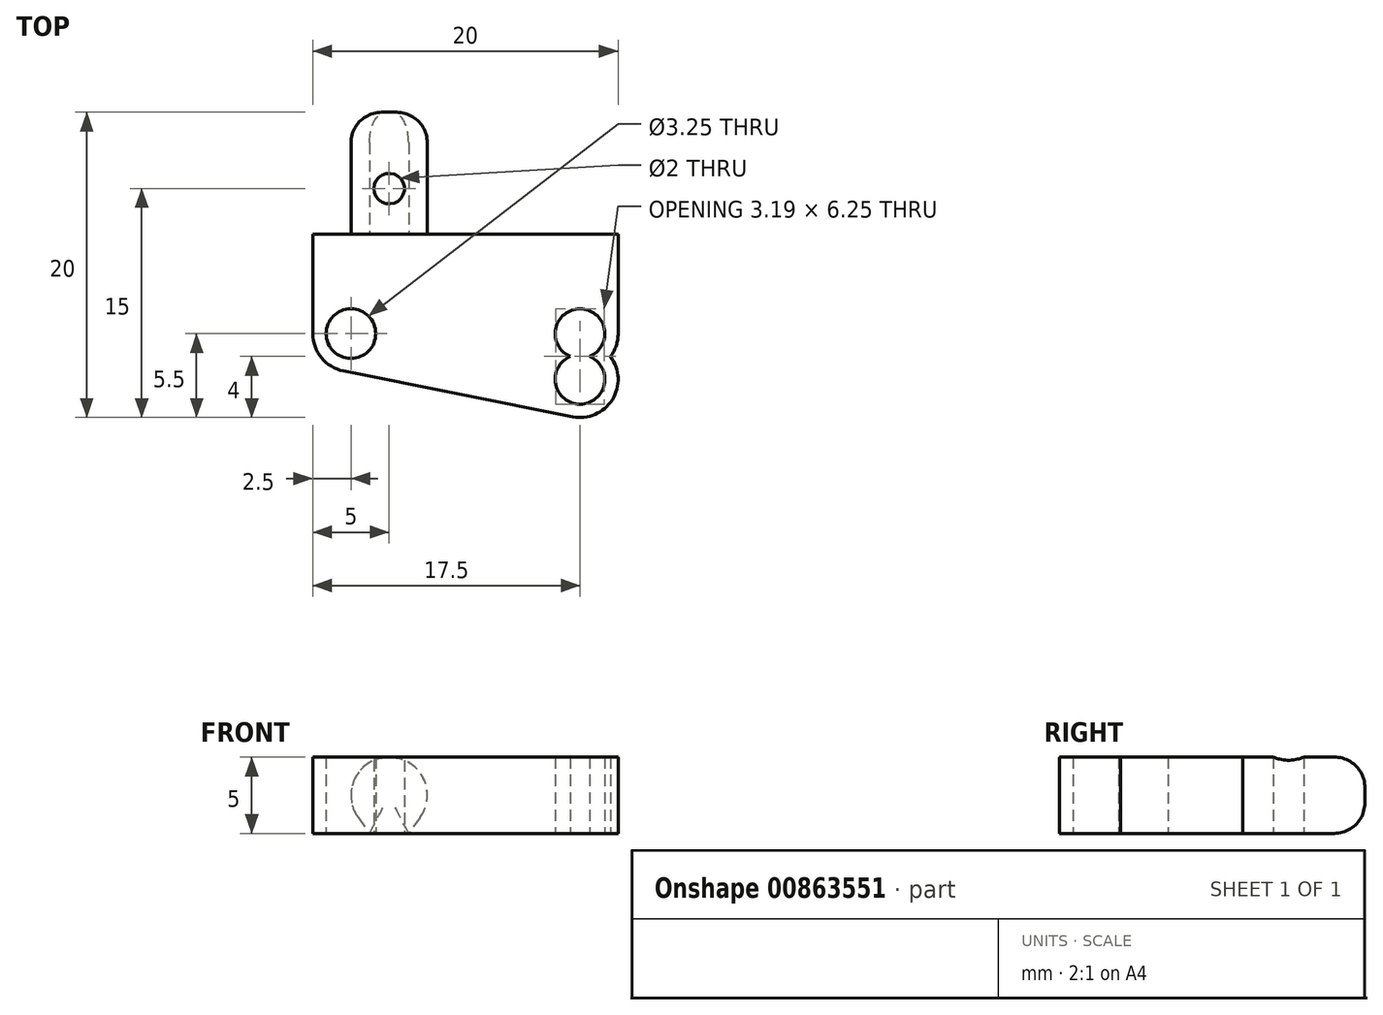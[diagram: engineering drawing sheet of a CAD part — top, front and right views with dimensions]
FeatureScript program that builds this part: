
annotation { "Feature Type Name" : "Feature", "Feature Type Description" : "" }
export const myFeature = defineFeature(function(context is Context, id is Id, definition is map)
    precondition{}
    {
        {
            var Q0;
            Q0=qCreatedBy(makeId("Top.planeOp"),FACE);
            var sketch = newSketch(context, id + "F0", { "sketchPlane" : qUnion([Q0])});
            skLineSegment(sketch, "E0", {"start": v(-7.5, 0) * mm, "end": v(7.5, 0) * mm, "construction": true});
            skCircle(sketch, "E1", {"center": v(-7.5, 0) * mm, "radius": 1.63 * mm});
            skArc(sketch, "E2", {"start": v(8.12, -1.5) * mm, "mid": v(7.5, 1.63) * mm, "end": v(6.87, -1.5) * mm});
            skArc(sketch, "E3", {"start": v(6.88, -1.5) * mm, "mid": v(7.5, -4.63) * mm, "end": v(8.12, -1.5) * mm});
            skLineSegment(sketch, "E4", {"start": v(7.5, -3) * mm, "end": v(7.5, 0) * mm, "construction": true});
            skArc(sketch, "E5", {"start": v(-10, 0) * mm, "mid": v(-9.43, -1.58) * mm, "end": v(-8, -2.45) * mm});
            skArc(sketch, "E6", {"start": v(9.5, -1.5) * mm, "mid": v(9.87, -0.8) * mm, "end": v(10, 0) * mm});
            skArc(sketch, "E7", {"start": v(7, -5.45) * mm, "mid": v(9.62, -4.33) * mm, "end": v(9.5, -1.5) * mm});
            skPoint(sketch, "E8", {"position": v(5.5, -1.5) * mm});
            skLineSegment(sketch, "E9", {"start": v(-8, -2.45) * mm, "end": v(7, -5.45) * mm});
            skLineSegment(sketch, "E10", {"start": v(-10, 6.5) * mm, "end": v(10, 6.5) * mm});
            skLineSegment(sketch, "E11", {"start": v(10, 6.5) * mm, "end": v(10, 0) * mm});
            skLineSegment(sketch, "E12", {"start": v(-10, 6.5) * mm, "end": v(-10, 0) * mm});
            skSolve(sketch);
        }
        {
            var Q0;
            Q0=makeQuery(id+"F0.imprint","IMPRINT",FACE,{"disambiguationData":[TD([[makeQuery(id+"F0.imprint","IMPRINT",EDGE,{"derivedFrom":sQuery(id+"F0.wireOp",EDGE,"E1")}),-1.0]])]});
            extrude(context, id + "F1", {"entities" : qUnion([Q0]), "depth" : 5 * mm, "offsetDistance" : 25 * mm});
        }
        {
            var Q0;
            Q0=makeQuery(id+"F1.opExtrude","SWEPT_FACE",FACE,{"disambiguationData":[OSD([sQuery(id+"F0.wireOp",EDGE,"E10")])]});
            var sketch = newSketch(context, id + "F2", { "sketchPlane" : qUnion([Q0])});
            skLineSegment(sketch, "E13", {"start": v(10, 2.5) * mm, "end": v(-10, 2.5) * mm, "construction": true});
            skArc(sketch, "E14", {"start": v(7.03, 1.03) * mm, "mid": v(5, 5) * mm, "end": v(2.97, 1.03) * mm});
            skLineSegment(sketch, "E15", {"start": v(2.97, 1.03) * mm, "end": v(3.72, 0) * mm});
            skLineSegment(sketch, "E16", {"start": v(7.03, 1.03) * mm, "end": v(6.28, 0) * mm});
            skLineSegment(sketch, "E17", {"start": v(5, 2.5) * mm, "end": v(5, 0) * mm, "construction": true});
            skLineSegment(sketch, "E18.0", {"start": v(10, 0) * mm, "end": v(6.28, 0) * mm});
            skLineSegment(sketch, "E19", {"start": v(6.28, 0) * mm, "end": v(3.72, 0) * mm});
            skLineSegment(sketch, "E20", {"start": v(3.72, 0) * mm, "end": v(-10, 0) * mm});
            skSolve(sketch);
        }
        {
            var Q0;
            Q0=makeQuery(id+"F2.imprint","IMPRINT",FACE,{"disambiguationData":[TD([[makeQuery(id+"F2.imprint","IMPRINT",EDGE,{"derivedFrom":sQuery(id+"F2.wireOp",EDGE,"E14")}),1.0]])]});
            extrude(context, id + "F3", {"entities" : qUnion([Q0]), "operationType" : NewBodyOperationType.ADD, "depth" : 8 * mm, "offsetDistance" : 25 * mm});
        }
        {
            var Q0;
            Q0=makeQuery(id+"F1.opExtrude","CAP_FACE",FACE,{"disambiguationData":[OSD([sQuery(id+"F0.wireOp",EDGE,"E1"),sQuery(id+"F0.wireOp",EDGE,"E2"),sQuery(id+"F0.wireOp",EDGE,"E3"),sQuery(id+"F0.wireOp",EDGE,"E5"),sQuery(id+"F0.wireOp",EDGE,"E6"),sQuery(id+"F0.wireOp",EDGE,"E7"),sQuery(id+"F0.wireOp",EDGE,"E9"),sQuery(id+"F0.wireOp",EDGE,"E10"),sQuery(id+"F0.wireOp",EDGE,"E11"),sQuery(id+"F0.wireOp",EDGE,"E12")])],"isStart":false});
            var sketch = newSketch(context, id + "F4", { "sketchPlane" : qUnion([Q0])});
            skLineSegment(sketch, "E21", {"start": v(-10, 5) * mm, "end": v(10, 5) * mm});
            skSolve(sketch);
        }
        {
            var Q0;
            Q0=makeQuery(id+"F3.opExtrude","CAP_FACE",FACE,{"disambiguationData":[OSD([sQuery(id+"F2.wireOp",EDGE,"E14"),sQuery(id+"F2.wireOp",EDGE,"E15"),sQuery(id+"F2.wireOp",EDGE,"E16"),sQuery(id+"F2.wireOp",EDGE,"E19")])],"isStart":false});
            fillet(context, id + "F5", {"entities" : qUnion([Q0]), "radius" : 2 * mm, "tangentPropagation" : true, "allowEdgeOverflow" : false});
        }
        {
            var Q0;
            Q0=makeQuery(id+"F3.boolean.opBoolean","MERGE",FACE,{"derivedFrom":[makeQuery(id+"F1.opExtrude","CAP_FACE",FACE,{"disambiguationData":[OSD([sQuery(id+"F0.wireOp",EDGE,"E1"),sQuery(id+"F0.wireOp",EDGE,"E2"),sQuery(id+"F0.wireOp",EDGE,"E3"),sQuery(id+"F0.wireOp",EDGE,"E5"),sQuery(id+"F0.wireOp",EDGE,"E6"),sQuery(id+"F0.wireOp",EDGE,"E7"),sQuery(id+"F0.wireOp",EDGE,"E9"),sQuery(id+"F0.wireOp",EDGE,"E10"),sQuery(id+"F0.wireOp",EDGE,"E11"),sQuery(id+"F0.wireOp",EDGE,"E12")])],"isStart":true}),makeQuery(id+"F3.opExtrude","SWEPT_FACE",FACE,{"disambiguationData":[OSD([sQuery(id+"F2.wireOp",EDGE,"E19")])]})]});
            var sketch = newSketch(context, id + "F6", { "sketchPlane" : qUnion([Q0])});
            skLineSegment(sketch, "E22", {"start": v(-3.72, -6.5) * mm, "end": v(-6.28, -6.5) * mm, "construction": true});
            skLineSegment(sketch, "E23", {"start": v(-5, -12.5) * mm, "end": v(-5, -6.5) * mm, "construction": true});
            skCircle(sketch, "E24", {"center": v(-5, -9.5) * mm, "radius": 1 * mm});
            skSolve(sketch);
        }
        {
            var Q0;
            Q0=makeQuery(id+"F6.imprint","IMPRINT",FACE,{"disambiguationData":[TD([[makeQuery(id+"F6.imprint","IMPRINT",EDGE,{"derivedFrom":sQuery(id+"F6.wireOp",EDGE,"E24")}),1.0]])]});
            extrude(context, id + "F7", {"entities" : qUnion([Q0]), "operationType" : NewBodyOperationType.REMOVE, "endBound" : BoundingType.THROUGH_ALL, "oppositeDirection" : true, "depth" : 25 * mm, "offsetDistance" : 25 * mm});
        }
    });
